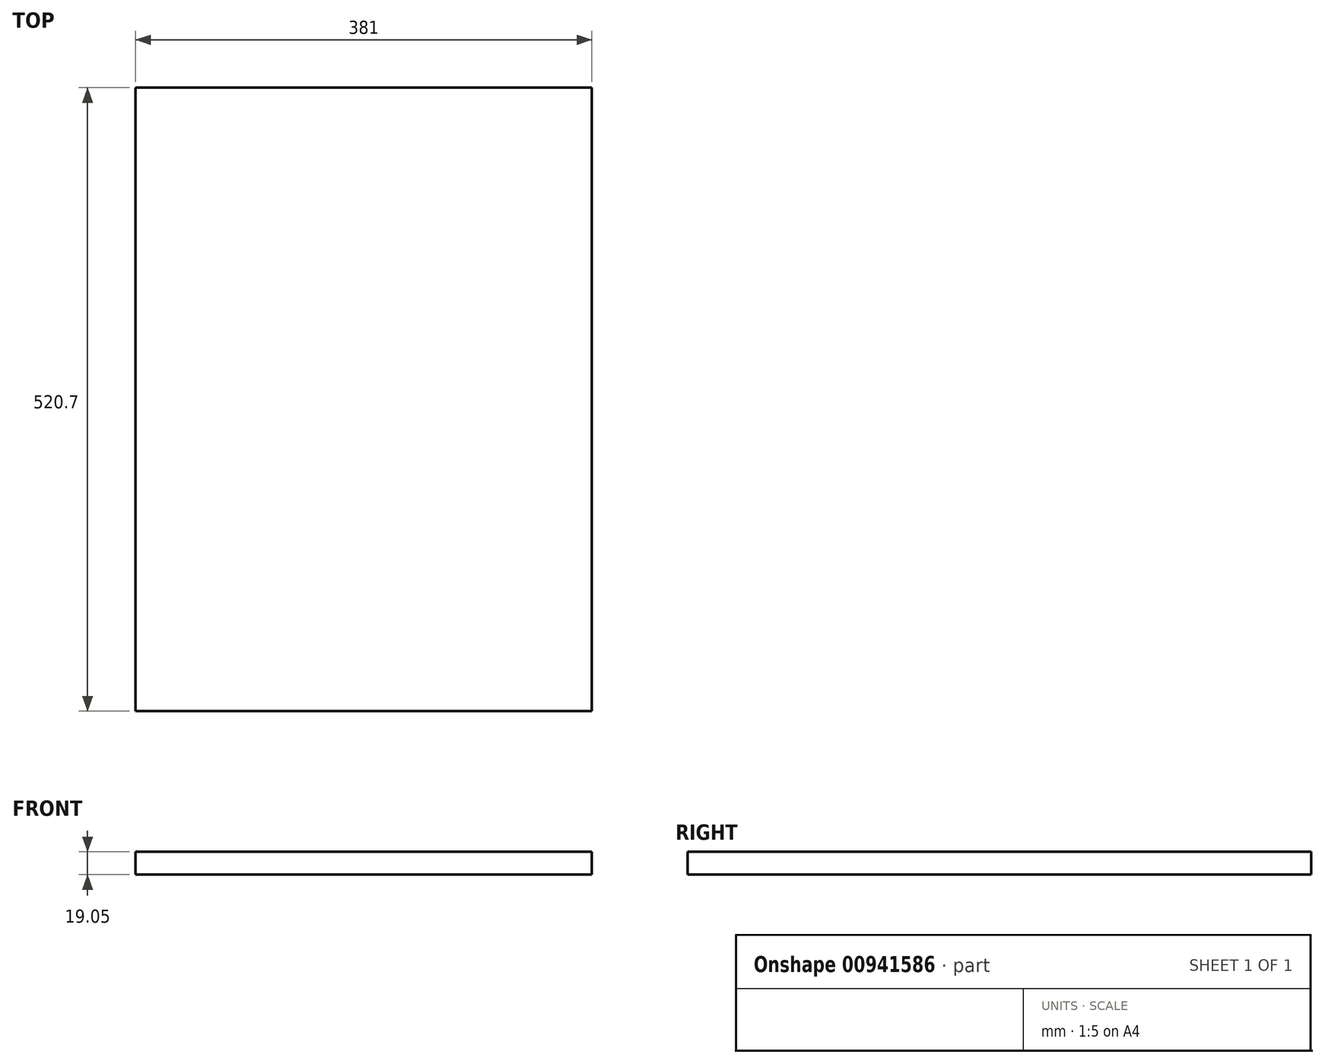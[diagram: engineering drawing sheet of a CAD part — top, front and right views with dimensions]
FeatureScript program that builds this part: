
annotation { "Feature Type Name" : "Feature", "Feature Type Description" : "" }
export const myFeature = defineFeature(function(context is Context, id is Id, definition is map)
    precondition{}
    {
        {
            var Q0;
            Q0=qCreatedBy(makeId("Front.planeOp"),FACE);
            var sketch = newSketch(context, id + "F0", { "sketchPlane" : qUnion([Q0])});
            skLineSegment(sketch, "E0.bottom", {"start": v(0, 0) * mm, "end": v(381, 0) * mm});
            skLineSegment(sketch, "E0.top", {"start": v(0, -19.05) * mm, "end": v(381, -19.05) * mm});
            skLineSegment(sketch, "E0.left", {"start": v(0, 0) * mm, "end": v(0, -19.05) * mm});
            skLineSegment(sketch, "E0.right", {"start": v(381, 0) * mm, "end": v(381, -19.05) * mm});
            skSolve(sketch);
        }
        {
            var Q0;
            Q0 = qSketchRegion(id + "F0", true);
            extrude(context, id + "F1", {"entities" : qUnion([Q0]), "depth" : 520.7 * mm, "offsetDistance" : 25.4 * mm});
        }
    });
